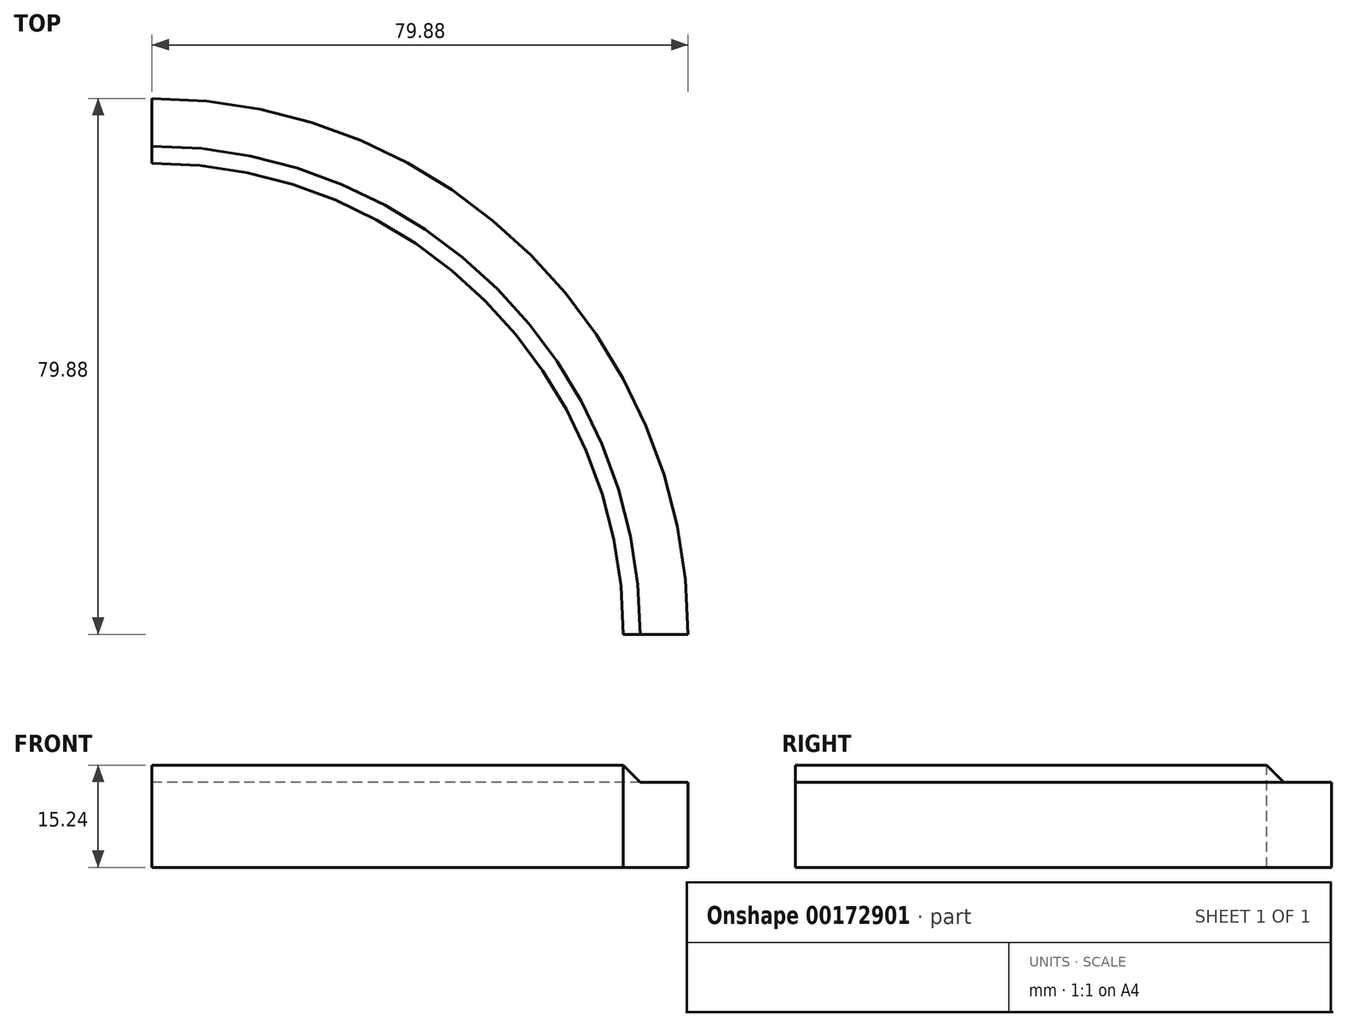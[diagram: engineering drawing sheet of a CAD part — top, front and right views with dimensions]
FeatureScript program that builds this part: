
annotation { "Feature Type Name" : "Feature", "Feature Type Description" : "" }
export const myFeature = defineFeature(function(context is Context, id is Id, definition is map)
    precondition{}
    {
        {
            var Q0;
            Q0=qCreatedBy(makeId("Right.planeOp"),FACE);
            var sketch = newSketch(context, id + "F0", { "sketchPlane" : qUnion([Q0])});
            skLineSegment(sketch, "E0", {"start": v(70.23, 0) * mm, "end": v(70.23, 15.24) * mm});
            skLineSegment(sketch, "E1", {"start": v(79.88, 12.7) * mm, "end": v(79.88, 0) * mm});
            skLineSegment(sketch, "E2", {"start": v(79.88, 0) * mm, "end": v(70.23, 0) * mm});
            skLineSegment(sketch, "E3", {"start": v(0, 56.17) * mm, "end": v(0, -44.6) * mm, "construction": true});
            skLineSegment(sketch, "E4", {"start": v(70.23, 15.24) * mm, "end": v(72.77, 12.7) * mm});
            skLineSegment(sketch, "E5", {"start": v(72.77, 12.7) * mm, "end": v(79.88, 12.7) * mm});
            skSolve(sketch);
        }
        {
            var Q0;
            Q0 = qSketchRegion(id + "F0", true);
            var Q1;
            Q1=sQuery(id+"F0.wireOp",EDGE,"E3");
            revolve(context, id + "F1", {"entities" : qUnion([Q0]), "axis" : qUnion([Q1]), "revolveType" : RevolveType.ONE_DIRECTION, "angle" : 90 * degree});
        }
    });
